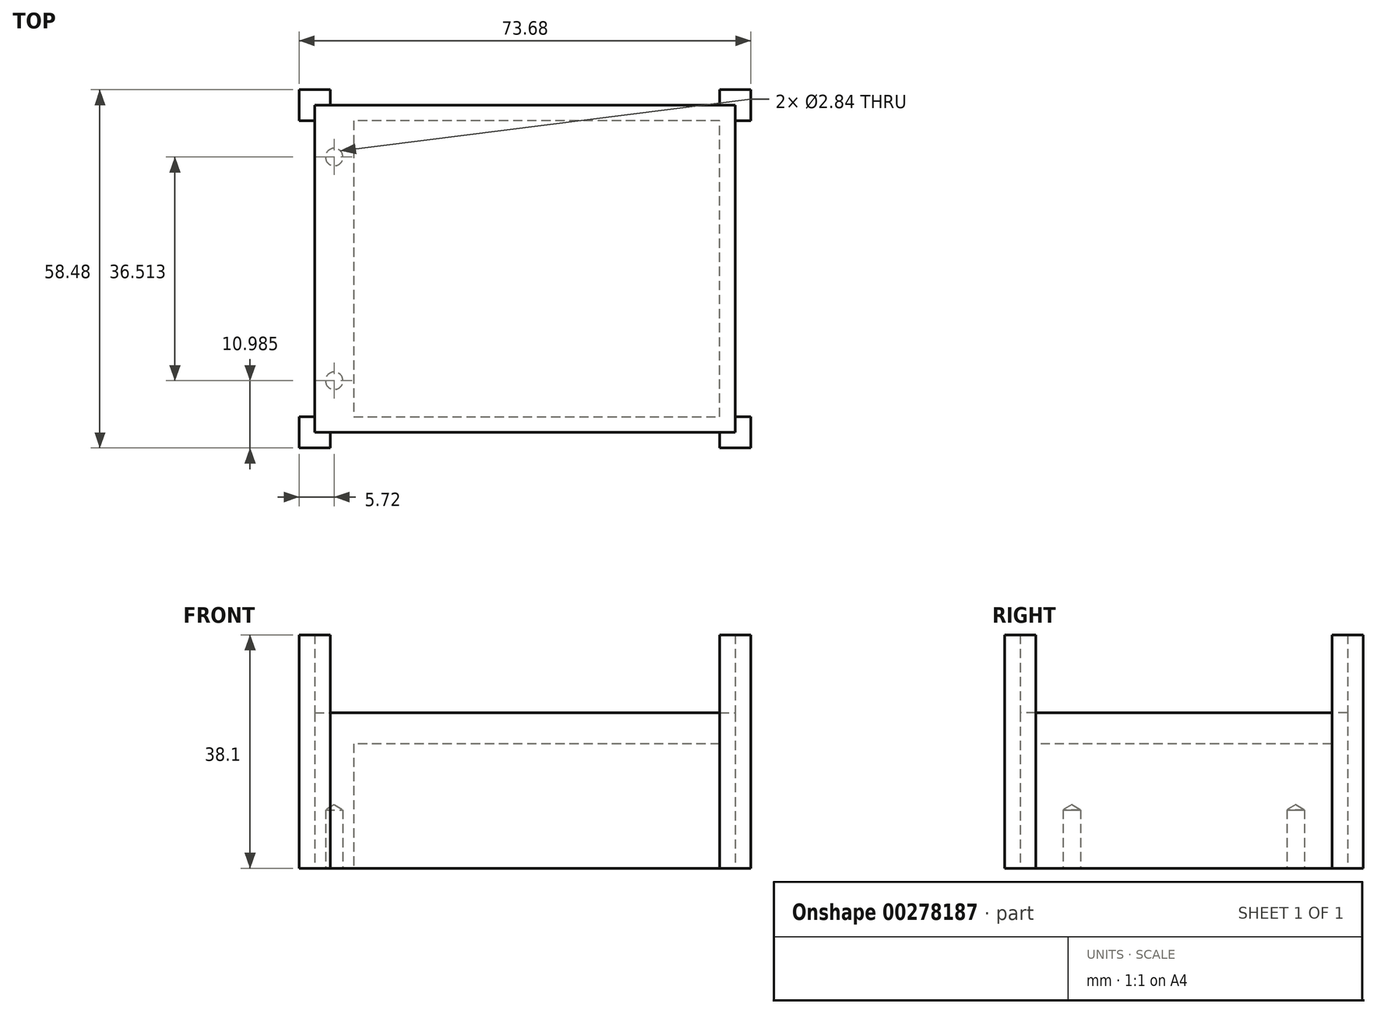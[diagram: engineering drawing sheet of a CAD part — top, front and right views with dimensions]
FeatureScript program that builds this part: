
annotation { "Feature Type Name" : "Feature", "Feature Type Description" : "" }
export const myFeature = defineFeature(function(context is Context, id is Id, definition is map)
    precondition{}
    {
        {
            var Q0;
            Q0=qCreatedBy(makeId("Top.planeOp"),FACE);
            var sketch = newSketch(context, id + "F0", { "sketchPlane" : qUnion([Q0])});
            skLineSegment(sketch, "E0.bottom", {"start": v(-35.76, 14.81) * mm, "end": v(32.84, 14.81) * mm});
            skLineSegment(sketch, "E0.top", {"start": v(-35.76, -38.59) * mm, "end": v(32.84, -38.59) * mm});
            skLineSegment(sketch, "E0.left", {"start": v(-35.76, 14.81) * mm, "end": v(-35.76, -38.59) * mm});
            skLineSegment(sketch, "E0.right", {"start": v(32.84, 14.81) * mm, "end": v(32.84, -38.59) * mm});
            skSolve(sketch);
        }
        {
            var Q0;
            Q0 = qSketchRegion(id + "F0", true);
            extrude(context, id + "F1", {"entities" : qUnion([Q0]), "depth" : 25.4 * mm});
        }
        {
            var Q0;
            Q0=makeQuery(id+"F1.opExtrude","CAP_FACE",FACE,{"disambiguationData":[OSD([sQuery(id+"F0.wireOp",EDGE,"E0.bottom"),sQuery(id+"F0.wireOp",EDGE,"E0.top"),sQuery(id+"F0.wireOp",EDGE,"E0.left"),sQuery(id+"F0.wireOp",EDGE,"E0.right")])],"isStart":true});
            var sketch = newSketch(context, id + "F2", { "sketchPlane" : qUnion([Q0])});
            skPoint(sketch, "E1", {"position": v(-33.22, 38.59) * mm});
            skPoint(sketch, "E2", {"position": v(-35.76, 36.05) * mm});
            skPoint(sketch, "E3", {"position": v(-35.76, 38.59) * mm});
            skPoint(sketch, "E4", {"position": v(-38.3, 36.05) * mm});
            skPoint(sketch, "E5", {"position": v(-33.22, 41.13) * mm});
            skPoint(sketch, "E6", {"position": v(-38.3, 41.13) * mm});
            skLineSegment(sketch, "E7", {"start": v(-33.22, 38.59) * mm, "end": v(-33.22, 41.13) * mm});
            skLineSegment(sketch, "E8", {"start": v(-38.3, 41.13) * mm, "end": v(-38.3, 36.05) * mm});
            skLineSegment(sketch, "E9", {"start": v(-38.3, 36.05) * mm, "end": v(-35.76, 36.05) * mm});
            skLineSegment(sketch, "E10", {"start": v(-38.3, 41.13) * mm, "end": v(-33.22, 41.13) * mm});
            skPoint(sketch, "E11", {"position": v(30.3, 38.59) * mm});
            skPoint(sketch, "E12", {"position": v(32.84, 36.05) * mm});
            skPoint(sketch, "E13", {"position": v(35.38, 36.05) * mm});
            skPoint(sketch, "E14", {"position": v(30.3, 41.13) * mm});
            skPoint(sketch, "E15", {"position": v(35.38, 41.13) * mm});
            skPoint(sketch, "E16", {"position": v(32.84, -12.27) * mm});
            skPoint(sketch, "E17", {"position": v(30.3, -14.81) * mm});
            skPoint(sketch, "E18", {"position": v(30.3, -17.35) * mm});
            skPoint(sketch, "E19", {"position": v(35.38, -12.27) * mm});
            skPoint(sketch, "E20", {"position": v(35.38, -17.35) * mm});
            skPoint(sketch, "E21", {"position": v(-35.76, -12.27) * mm});
            skPoint(sketch, "E22", {"position": v(-38.3, -12.27) * mm});
            skPoint(sketch, "E23", {"position": v(-33.22, -14.81) * mm});
            skPoint(sketch, "E24", {"position": v(-33.22, -17.35) * mm});
            skPoint(sketch, "E25", {"position": v(-38.3, -17.35) * mm});
            skLineSegment(sketch, "E26", {"start": v(30.3, 38.59) * mm, "end": v(30.3, 41.13) * mm});
            skLineSegment(sketch, "E27", {"start": v(30.3, 41.13) * mm, "end": v(35.38, 41.13) * mm});
            skLineSegment(sketch, "E28", {"start": v(35.38, 41.13) * mm, "end": v(35.38, 36.05) * mm});
            skLineSegment(sketch, "E29", {"start": v(32.84, 36.05) * mm, "end": v(35.38, 36.05) * mm});
            skLineSegment(sketch, "E30", {"start": v(30.3, 38.59) * mm, "end": v(32.84, 38.59) * mm});
            skLineSegment(sketch, "E31", {"start": v(32.84, 38.59) * mm, "end": v(32.84, 36.05) * mm});
            skLineSegment(sketch, "E32", {"start": v(35.38, -12.27) * mm, "end": v(32.84, -12.27) * mm});
            skLineSegment(sketch, "E33", {"start": v(35.38, -17.35) * mm, "end": v(35.38, -12.27) * mm});
            skLineSegment(sketch, "E34", {"start": v(30.3, -14.81) * mm, "end": v(32.84, -14.81) * mm});
            skLineSegment(sketch, "E35", {"start": v(32.84, -14.81) * mm, "end": v(32.84, -12.27) * mm});
            skLineSegment(sketch, "E36", {"start": v(30.3, -17.35) * mm, "end": v(30.3, -14.81) * mm});
            skLineSegment(sketch, "E37", {"start": v(30.3, -17.35) * mm, "end": v(35.38, -17.35) * mm});
            skLineSegment(sketch, "E38", {"start": v(-38.3, -12.27) * mm, "end": v(-35.76, -12.27) * mm});
            skLineSegment(sketch, "E39", {"start": v(-38.3, -12.27) * mm, "end": v(-38.3, -17.35) * mm});
            skLineSegment(sketch, "E40", {"start": v(-33.22, -17.35) * mm, "end": v(-38.3, -17.35) * mm});
            skLineSegment(sketch, "E41", {"start": v(-33.22, -14.81) * mm, "end": v(-33.22, -17.35) * mm});
            skLineSegment(sketch, "E42", {"start": v(-35.76, -12.27) * mm, "end": v(-35.76, -14.81) * mm});
            skLineSegment(sketch, "E43", {"start": v(-35.76, -14.81) * mm, "end": v(-33.22, -14.81) * mm});
            skSolve(sketch);
        }
        {
            var Q0;
            {var subQ4=sQuery(id+"F2.wireOp",EDGE,"E7");Q0=makeQuery(id+"F2.imprint","IMPRINT",FACE,{"disambiguationData":[TD([[makeQuery(id+"F2.imprint","IMPRINT",EDGE,{"derivedFrom":subQ4}),1.0]])]});}
            extrude(context, id + "F3", {"entities" : qUnion([Q0]), "operationType" : NewBodyOperationType.ADD, "oppositeDirection" : true, "depth" : 38.1 * mm});
        }
        {
            var Q0;
            Q0=makeQuery(id+"F2.imprint","IMPRINT",FACE,{"disambiguationData":[TD([[makeQuery(id+"F2.imprint","IMPRINT",EDGE,{"derivedFrom":sQuery(id+"F2.wireOp",EDGE,"E26")}),-1.0]])]});
            var Q1;
            Q1=makeQuery(id+"F2.imprint","IMPRINT",FACE,{"disambiguationData":[TD([[makeQuery(id+"F2.imprint","IMPRINT",EDGE,{"derivedFrom":sQuery(id+"F2.wireOp",EDGE,"E38")}),-1.0]])]});
            var Q2;
            Q2=makeQuery(id+"F2.imprint","IMPRINT",FACE,{"disambiguationData":[TD([[makeQuery(id+"F2.imprint","IMPRINT",EDGE,{"derivedFrom":sQuery(id+"F2.wireOp",EDGE,"E32")}),1.0]])]});
            extrude(context, id + "F4", {"entities" : qUnion([Q0, Q1, Q2]), "operationType" : NewBodyOperationType.ADD, "oppositeDirection" : true, "depth" : 38.1 * mm});
        }
        {
            var Q0;
            Q0=qCreatedBy(makeId("Front.planeOp"),FACE);
            var sketch = newSketch(context, id + "F5", { "sketchPlane" : qUnion([Q0])});
            skLineSegment(sketch, "E44", {"start": v(35.75, 5.08) * mm, "end": v(-39.07, 5.08) * mm, "construction": true});
            skSolve(sketch);
        }
        {
            var Q0;
            Q0=makeQuery(id+"F4.opExtrude","SWEPT_FACE",FACE,{"disambiguationData":[OSD([sQuery(id+"F2.wireOp",EDGE,"E27")])]});
            var sketch = newSketch(context, id + "F6", { "sketchPlane" : qUnion([Q0])});
            skLineSegment(sketch, "E45", {"start": v(35.38, 5.08) * mm, "end": v(-43.23, 5.08) * mm, "construction": true});
            skSolve(sketch);
        }
        {
            var Q0;
            Q0=qCreatedBy(makeId("Top.planeOp"),FACE);
            var sketch = newSketch(context, id + "F7", { "sketchPlane" : qUnion([Q0])});
            skLineSegment(sketch, "E46", {"start": v(-29.4, 12.27) * mm, "end": v(-29.4, -36.05) * mm});
            skLineSegment(sketch, "E47", {"start": v(-29.4, -36.05) * mm, "end": v(30.3, -36.05) * mm});
            skLineSegment(sketch, "E48", {"start": v(30.3, -36.05) * mm, "end": v(30.3, 12.27) * mm});
            skLineSegment(sketch, "E49", {"start": v(30.3, 12.27) * mm, "end": v(-29.4, 12.27) * mm});
            skPoint(sketch, "E50", {"position": v(-32.58, -30.14) * mm});
            skPoint(sketch, "E51", {"position": v(-32.58, 6.37) * mm});
            skSolve(sketch);
        }
        {
            var Q0;
            Q0 = qSketchRegion(id + "F7", true);
            extrude(context, id + "F8", {"entities" : qUnion([Q0]), "operationType" : NewBodyOperationType.REMOVE, "depth" : 20.32 * mm});
        }
        {
            var Q0;
            Q0=sQuery(id+"F7.wireOp",VERTEX,"E50");
            var Q1;
            Q1=sQuery(id+"F7.wireOp",VERTEX,"E51");
            var Q2;
            Q2=makeQuery(id+"F1.opExtrude","SWEPT_BODY",BODY,{"disambiguationData":[OSD([sQuery(id+"F0.wireOp",EDGE,"E0.bottom"),sQuery(id+"F0.wireOp",EDGE,"E0.top"),sQuery(id+"F0.wireOp",EDGE,"E0.left"),sQuery(id+"F0.wireOp",EDGE,"E0.right")])]});
            hole(context, id + "F9", {"style" : HoleStyle.SIMPLE, "endStyle" : HoleEndStyle.BLIND, "oppositeDirection" : true, "holeDiameter" : 2.84 * mm, "holeDepth" : 9.52 * mm, "tappedDepth" : 12.7 * mm, "tapClearance" : 3, "locations" : qUnion([Q0, Q1]), "scope" : qUnion([Q2])});
        }
    });
